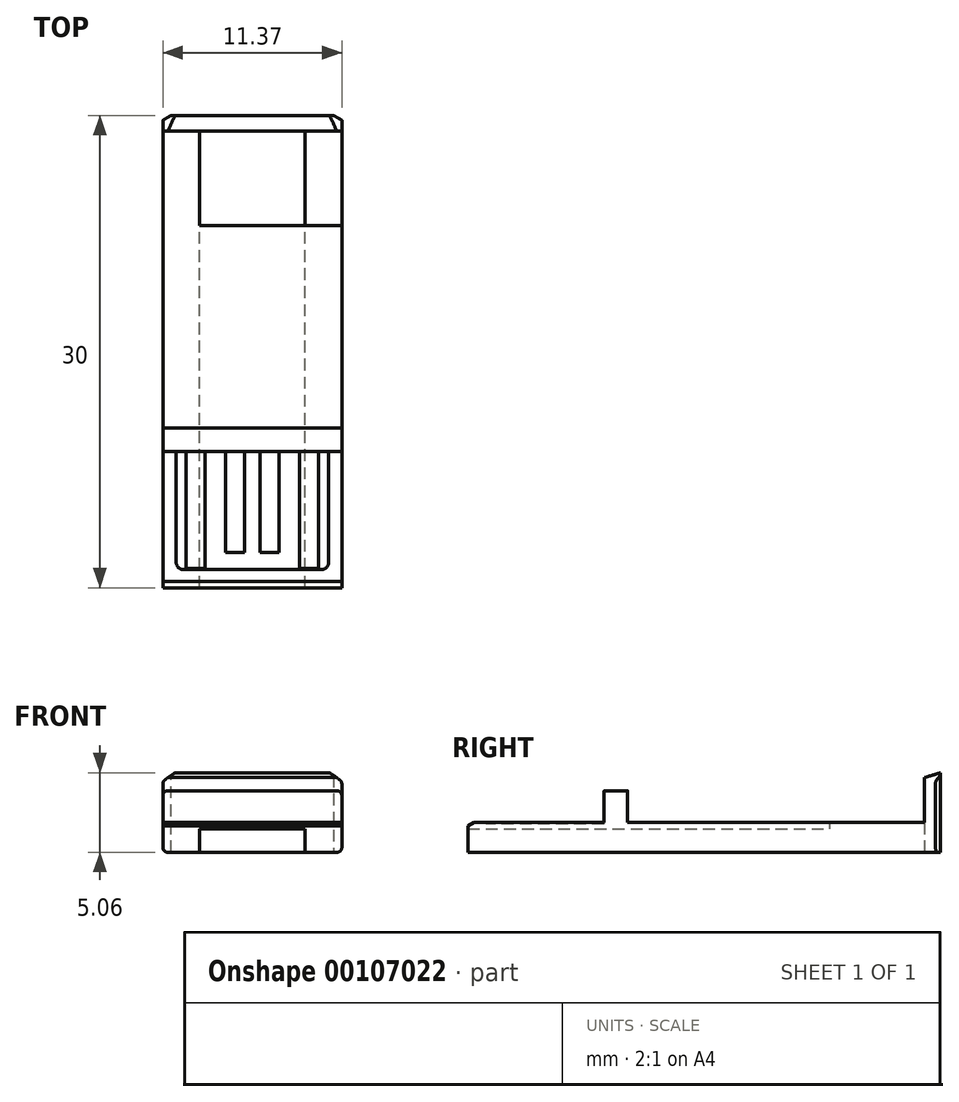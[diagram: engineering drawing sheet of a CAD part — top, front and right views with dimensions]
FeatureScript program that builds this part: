
annotation { "Feature Type Name" : "Feature", "Feature Type Description" : "" }
export const myFeature = defineFeature(function(context is Context, id is Id, definition is map)
    precondition{}
    {
        {
            var Q0;
            Q0=qCreatedBy(makeId("Front.planeOp"),FACE);
            var sketch = newSketch(context, id + "F0", { "sketchPlane" : qUnion([Q0])});
            skLineSegment(sketch, "E0.bottom", {"start": v(0, 0) * mm, "end": v(2.33, 0) * mm});
            skLineSegment(sketch, "E0.top", {"start": v(0, 1.92) * mm, "end": v(11.37, 1.92) * mm});
            skLineSegment(sketch, "E0.left", {"start": v(0, 0) * mm, "end": v(0, 1.92) * mm});
            skLineSegment(sketch, "E0.right", {"start": v(11.37, 0) * mm, "end": v(11.37, 1.92) * mm});
            skLineSegment(sketch, "E1.top", {"start": v(2.33, 1.5) * mm, "end": v(9.04, 1.5) * mm});
            skLineSegment(sketch, "E1.left", {"start": v(2.33, 0) * mm, "end": v(2.33, 1.5) * mm});
            skLineSegment(sketch, "E1.right", {"start": v(9.04, 0) * mm, "end": v(9.04, 1.5) * mm});
            skLineSegment(sketch, "E2.trimOffspring", {"start": v(9.04, 0) * mm, "end": v(11.37, 0) * mm});
            skSolve(sketch);
        }
        {
            var Q0;
            Q0=qSketchRegion(id+"F0",true);
            extrude(context, id + "F1", {"entities" : qUnion([Q0]), "depth" : 23 * mm});
        }
        {
            var Q0;
            Q0=makeQuery(id+"F1.opExtrude","SWEPT_EDGE",EDGE,{"disambiguationData":[OSD([sQuery(id+"F0.wireOp",EDGE,"E0.right"),sQuery(id+"F0.wireOp",EDGE,"E2.trimOffspring")])]});
            var Q1;
            Q1=makeQuery(id+"F1.opExtrude","SWEPT_EDGE",EDGE,{"disambiguationData":[OSD([sQuery(id+"F0.wireOp",EDGE,"E0.bottom"),sQuery(id+"F0.wireOp",EDGE,"E0.left")])]});
            fillet(context, id + "F2", {"entities" : qUnion([Q0, Q1]), "radius" : .325 * mm, "tangentPropagation" : true, "allowEdgeOverflow" : false});
        }
        {
            var Q0;
            Q0=makeQuery(id+"F1.opExtrude","CAP_EDGE",EDGE,{"disambiguationData":[OSD([sQuery(id+"F0.wireOp",EDGE,"E0.top")])],"isStart":false});
            chamfer(context, id + "F3", {"entities" : qUnion([Q0]), "chamferType" : ChamferType.OFFSET_ANGLE, "width" : .4 * mm, "oppositeDirection" : false, "angle" : 30 * degree, "tangentPropagation" : true});
        }
        {
            var Q0;
            Q0=qCreatedBy(makeId("Front.planeOp"),FACE);
            var sketch = newSketch(context, id + "F4", { "sketchPlane" : qUnion([Q0])});
            skLineSegment(sketch, "E3.0", {"start": v(0.32, 0) * mm, "end": v(2.33, 0) * mm});
            skArc(sketch, "E3.1", {"start": v(0.32, 0) * mm, "mid": v(0.1, 0.1) * mm, "end": v(0, 0.33) * mm});
            skLineSegment(sketch, "E3.2", {"start": v(0, 0.33) * mm, "end": v(0, 1.92) * mm});
            skLineSegment(sketch, "E4", {"start": v(2.33, 0) * mm, "end": v(2.33, 1.92) * mm});
            skLineSegment(sketch, "E5", {"start": v(2.33, 1.92) * mm, "end": v(0, 1.92) * mm});
            skLineSegment(sketch, "E6.0", {"start": v(9.04, 0) * mm, "end": v(11.04, 0) * mm});
            skArc(sketch, "E6.1", {"start": v(11.37, 0.33) * mm, "mid": v(11.27, 0.1) * mm, "end": v(11.04, 0) * mm});
            skLineSegment(sketch, "E6.2", {"start": v(11.37, 0.33) * mm, "end": v(11.37, 1.92) * mm});
            skLineSegment(sketch, "E7", {"start": v(9.04, 0) * mm, "end": v(9.04, 1.9) * mm});
            skLineSegment(sketch, "E8", {"start": v(9.04, 1.9) * mm, "end": v(11.37, 1.92) * mm});
            skSolve(sketch);
        }
        {
            var Q0;
            Q0=qSketchRegion(id+"F4",true);
            extrude(context, id + "F5", {"entities" : qUnion([Q0]), "operationType" : NewBodyOperationType.ADD, "oppositeDirection" : true, "depth" : 7 * mm});
        }
        {
            var Q0;
            Q0=makeQuery(id+"F5.opExtrude","CAP_FACE",FACE,{"disambiguationData":[OSD([sQuery(id+"F4.wireOp",EDGE,"E3.0"),sQuery(id+"F4.wireOp",EDGE,"E3.1"),sQuery(id+"F4.wireOp",EDGE,"E3.2"),sQuery(id+"F4.wireOp",EDGE,"E4"),sQuery(id+"F4.wireOp",EDGE,"E5")])],"isStart":false});
            var sketch = newSketch(context, id + "F6", { "sketchPlane" : qUnion([Q0])});
            skLineSegment(sketch, "E9.bottom", {"start": v(0, 0) * mm, "end": v(-11.37, 0) * mm});
            skLineSegment(sketch, "E9.left", {"start": v(0, 0) * mm, "end": v(0, 4.5) * mm});
            skLineSegment(sketch, "E9.right", {"start": v(-11.37, 0) * mm, "end": v(-11.37, 4.5) * mm});
            skArc(sketch, "E10", {"start": v(0, 4.5) * mm, "mid": v(-0.41, 4.81) * mm, "end": v(-0.85, 5.1) * mm});
            skLineSegment(sketch, "E11", {"start": v(-10.52, 5.1) * mm, "end": v(-0.85, 5.1) * mm});
            skArc(sketch, "E12.trimOffspring", {"start": v(-10.52, 5.1) * mm, "mid": v(-10.96, 4.81) * mm, "end": v(-11.37, 4.5) * mm});
            skSolve(sketch);
        }
        {
            var Q0;
            Q0=qSketchRegion(id+"F6",true);
            extrude(context, id + "F7", {"entities" : qUnion([Q0]), "operationType" : NewBodyOperationType.ADD, "oppositeDirection" : true, "depth" : 1 * mm});
        }
        {
            var Q0;
            Q0=makeQuery(id+"F7.opExtrude","SWEPT_EDGE",EDGE,{"disambiguationData":[OSD([sQuery(id+"F6.wireOp",EDGE,"E9.bottom"),sQuery(id+"F6.wireOp",EDGE,"E9.left")])]});
            var Q1;
            Q1=makeQuery(id+"F7.opExtrude","SWEPT_EDGE",EDGE,{"disambiguationData":[OSD([sQuery(id+"F6.wireOp",EDGE,"E9.bottom"),sQuery(id+"F6.wireOp",EDGE,"E9.right")])]});
            var Q2;
            Q2=makeQuery(id+"F7.opExtrude","SWEPT_EDGE",EDGE,{"disambiguationData":[OSD([sQuery(id+"F6.wireOp",EDGE,"E9.top"),sQuery(id+"F6.wireOp",EDGE,"E9.left")])]});
            var Q3;
            Q3=makeQuery(id+"F7.opExtrude","SWEPT_EDGE",EDGE,{"disambiguationData":[OSD([sQuery(id+"F6.wireOp",EDGE,"E9.top"),sQuery(id+"F6.wireOp",EDGE,"E9.right")])]});
            fillet(context, id + "F8", {"entities" : qUnion([Q0, Q1, Q2, Q3]), "radius" : .325 * mm, "allowEdgeOverflow" : false});
        }
        {
            var Q0;
            Q0=makeQuery(id+"F1.opExtrude","SWEPT_FACE",FACE,{"disambiguationData":[OSD([sQuery(id+"F0.wireOp",EDGE,"E0.top")])]});
            var sketch = newSketch(context, id + "F9", { "sketchPlane" : qUnion([Q0])});
            skLineSegment(sketch, "E13.bottom", {"start": v(0, -14.35) * mm, "end": v(11.37, -14.35) * mm});
            skLineSegment(sketch, "E13.top", {"start": v(0, -12.85) * mm, "end": v(11.37, -12.85) * mm});
            skLineSegment(sketch, "E13.left", {"start": v(0, -14.35) * mm, "end": v(0, -12.85) * mm});
            skLineSegment(sketch, "E13.right", {"start": v(11.37, -14.35) * mm, "end": v(11.37, -12.85) * mm});
            skSolve(sketch);
        }
        {
            var Q0;
            Q0=qSketchRegion(id+"F9",true);
            var Q1;
            Q1=makeQuery(id+"F7.opExtrude","SWEPT_FACE",FACE,{"disambiguationData":[OSD([sQuery(id+"F6.wireOp",EDGE,"E9.top")])]});
            extrude(context, id + "F10", {"entities" : qUnion([Q0]), "operationType" : NewBodyOperationType.ADD, "endBoundEntityFace" : qUnion([Q1]), "depth" : 2 * mm});
        }
        {
            var Q0;
            Q0=makeQuery(id+"F10.opExtrude","TWEAK_EDGE",EDGE,{"derivedFrom":[makeQuery(id+"F7.opExtrude","SWEPT_FACE",FACE,{"disambiguationData":[OSD([sQuery(id+"F6.wireOp",EDGE,"E9.top")])]}),makeQuery(id+"F9.imprint","IMPRINT",EDGE,{"derivedFrom":sQuery(id+"F9.wireOp",EDGE,"E13.left")})]});
            var Q1;
            Q1=makeQuery(id+"F10.opExtrude","TWEAK_EDGE",EDGE,{"derivedFrom":[makeQuery(id+"F7.opExtrude","SWEPT_FACE",FACE,{"disambiguationData":[OSD([sQuery(id+"F6.wireOp",EDGE,"E9.top")])]}),makeQuery(id+"F9.imprint","IMPRINT",EDGE,{"derivedFrom":sQuery(id+"F9.wireOp",EDGE,"E13.right")})]});
            var Q2;
            Q2=makeQuery(id+"F10.opExtrude","CAP_EDGE",EDGE,{"disambiguationData":[OSD([sQuery(id+"F9.wireOp",EDGE,"E13.left")])],"isStart":false});
            var Q3;
            Q3=makeQuery(id+"F10.opExtrude","CAP_EDGE",EDGE,{"disambiguationData":[OSD([sQuery(id+"F9.wireOp",EDGE,"E13.right")])],"isStart":false});
            fillet(context, id + "F11", {"entities" : qUnion([Q0, Q1, Q2, Q3]), "radius" : .325 * mm, "tangentPropagation" : true, "allowEdgeOverflow" : false});
        }
        {
            var Q0;
            Q0=makeQuery(id+"F7.boolean.opBoolean","MERGE",EDGE,{"derivedFrom":[makeQuery(id+"F5.opExtrude","CAP_EDGE",EDGE,{"disambiguationData":[OSD([sQuery(id+"F4.wireOp",EDGE,"E6.2")])],"isStart":false}),makeQuery(id+"F7.opExtrude","CAP_EDGE",EDGE,{"disambiguationData":[OSD([sQuery(id+"F6.wireOp",EDGE,"E9.right")])],"isStart":true})]});
            var Q1;
            Q1=makeQuery(id+"F7.boolean.opBoolean","MERGE",EDGE,{"derivedFrom":[makeQuery(id+"F5.opExtrude","CAP_EDGE",EDGE,{"disambiguationData":[OSD([sQuery(id+"F4.wireOp",EDGE,"E3.2")])],"isStart":false}),makeQuery(id+"F7.opExtrude","CAP_EDGE",EDGE,{"disambiguationData":[OSD([sQuery(id+"F6.wireOp",EDGE,"E9.left")])],"isStart":true})]});
            chamfer(context, id + "F12", {"entities" : qUnion([Q0, Q1]), "chamferType" : ChamferType.OFFSET_ANGLE, "width" : .3 * mm, "oppositeDirection" : false, "angle" : 60 * degree});
        }
        {
            var Q0;
            {var subQ0=sQuery(id+"F0.wireOp",EDGE,"E0.top");Q0=makeQuery(id+"F10.boolean.opBoolean","SPLIT",FACE,{"disambiguationData":[TD([makeQuery(id+"F3.opChamfer","BLEND_FACE",FACE,{"disambiguationData":[OSD([subQ0])]})])],"derivedFrom":makeQuery(id+"F1.opExtrude","SWEPT_FACE",FACE,{"disambiguationData":[OSD([subQ0])]})});}
            var sketch = newSketch(context, id + "F13", { "sketchPlane" : qUnion([Q0])});
            skLineSegment(sketch, "E14", {"start": v(5.68, -14.35) * mm, "end": v(5.68, -22.6) * mm, "construction": true});
            skLineSegment(sketch, "E15.bottom", {"start": v(0.83, -14.35) * mm, "end": v(10.53, -14.35) * mm});
            skLineSegment(sketch, "E15.top", {"start": v(1.34, -21.85) * mm, "end": v(10.04, -21.85) * mm});
            skLineSegment(sketch, "E15.left", {"start": v(0.84, -14.35) * mm, "end": v(0.84, -21.35) * mm});
            skLineSegment(sketch, "E15.right", {"start": v(10.53, -14.35) * mm, "end": v(10.54, -21.35) * mm});
            skPoint(sketch, "E15.middle", {"position": v(5.69, -18.1) * mm});
            skPoint(sketch, "E16.visualSharp", {"position": v(0.84, -21.85) * mm});
            skArc(sketch, "E16.filletArc", {"start": v(0.84, -21.35) * mm, "mid": v(0.98, -21.7) * mm, "end": v(1.34, -21.85) * mm});
            skPoint(sketch, "E17.visualSharp", {"position": v(10.54, -21.85) * mm});
            skArc(sketch, "E17.filletArc", {"start": v(10.04, -21.85) * mm, "mid": v(10.39, -21.7) * mm, "end": v(10.54, -21.35) * mm});
            skSolve(sketch);
        }
        {
            var Q0;
            Q0 = qSketchRegion(id + "F13", true);
            extrude(context, id + "F14", {"entities" : qUnion([Q0]), "operationType" : NewBodyOperationType.REMOVE, "oppositeDirection" : true, "depth" : .1 * mm});
        }
        {
            var Q0;
            Q0=makeQuery(id+"F14.boolean.opBoolean","COPY",FACE,{"derivedFrom":makeQuery(id+"F14.opExtrude","CAP_FACE",FACE,{"disambiguationData":[OSD([sQuery(id+"F13.wireOp",EDGE,"E15.bottom"),sQuery(id+"F13.wireOp",EDGE,"E15.top"),sQuery(id+"F13.wireOp",EDGE,"E15.left"),sQuery(id+"F13.wireOp",EDGE,"E15.right"),sQuery(id+"F13.wireOp",EDGE,"E16.filletArc"),sQuery(id+"F13.wireOp",EDGE,"E17.filletArc")])],"isStart":false})});
            var sketch = newSketch(context, id + "F15", { "sketchPlane" : qUnion([Q0])});
            skLineSegment(sketch, "E18", {"start": v(5.69, -14.35) * mm, "end": v(5.69, -21.85) * mm, "construction": true});
            skLineSegment(sketch, "E19.bottom", {"start": v(3.98, -14.35) * mm, "end": v(5.19, -14.35) * mm});
            skLineSegment(sketch, "E19.top", {"start": v(3.99, -20.76) * mm, "end": v(5.19, -20.76) * mm});
            skLineSegment(sketch, "E19.left", {"start": v(3.98, -14.35) * mm, "end": v(3.98, -20.76) * mm});
            skLineSegment(sketch, "E19.right", {"start": v(5.19, -14.35) * mm, "end": v(5.19, -20.76) * mm});
            skLineSegment(sketch, "E20.bottom", {"start": v(1.48, -14.35) * mm, "end": v(2.69, -14.35) * mm});
            skLineSegment(sketch, "E20.top", {"start": v(1.49, -21.76) * mm, "end": v(2.69, -21.76) * mm});
            skLineSegment(sketch, "E20.left", {"start": v(1.48, -14.35) * mm, "end": v(1.49, -21.76) * mm});
            skLineSegment(sketch, "E20.right", {"start": v(2.69, -14.35) * mm, "end": v(2.69, -21.76) * mm});
            skLineSegment(sketch, "E21.MirrorCS", {"start": v(9.89, -21.76) * mm, "end": v(8.69, -21.76) * mm});
            skLineSegment(sketch, "E22.MirrorCS", {"start": v(9.89, -14.35) * mm, "end": v(8.69, -14.35) * mm});
            skLineSegment(sketch, "E23.MirrorCS", {"start": v(6.19, -14.35) * mm, "end": v(6.19, -20.76) * mm});
            skLineSegment(sketch, "E24.MirrorCS", {"start": v(7.39, -14.35) * mm, "end": v(7.39, -20.76) * mm});
            skLineSegment(sketch, "E25.MirrorCS", {"start": v(7.39, -20.76) * mm, "end": v(6.19, -20.76) * mm});
            skLineSegment(sketch, "E26.MirrorCS", {"start": v(7.39, -14.35) * mm, "end": v(6.19, -14.35) * mm});
            skLineSegment(sketch, "E27.MirrorCS", {"start": v(9.89, -14.35) * mm, "end": v(9.89, -21.76) * mm});
            skLineSegment(sketch, "E28.MirrorCS", {"start": v(8.69, -14.35) * mm, "end": v(8.69, -21.76) * mm});
            skSolve(sketch);
        }
        {
            var Q0;
            Q0 = qSketchRegion(id + "F15", true);
            var Q1;
            {var subQ0=sQuery(id+"F0.wireOp",EDGE,"E0.top");Q1=makeQuery(id+"F10.boolean.opBoolean","SPLIT",FACE,{"disambiguationData":[TD([makeQuery(id+"F3.opChamfer","BLEND_FACE",FACE,{"disambiguationData":[OSD([subQ0])]})])],"derivedFrom":makeQuery(id+"F1.opExtrude","SWEPT_FACE",FACE,{"disambiguationData":[OSD([subQ0])]})});}
            extrude(context, id + "F16", {"entities" : qUnion([Q0]), "operationType" : NewBodyOperationType.ADD, "endBound" : BoundingType.UP_TO_SURFACE, "endBoundEntityFace" : qUnion([Q1]), "depth" : 25 * mm});
        }
        {
            var Q0;
            Q0=makeQuery(id+"F7.opExtrude","CAP_EDGE",EDGE,{"disambiguationData":[OSD([sQuery(id+"F6.wireOp",EDGE,"E11")])],"isStart":false});
            chamfer(context, id + "F17", {"entities" : qUnion([Q0]), "chamferType" : ChamferType.OFFSET_ANGLE, "width" : .35 * mm, "oppositeDirection" : false, "angle" : 73 * degree});
        }
    });
